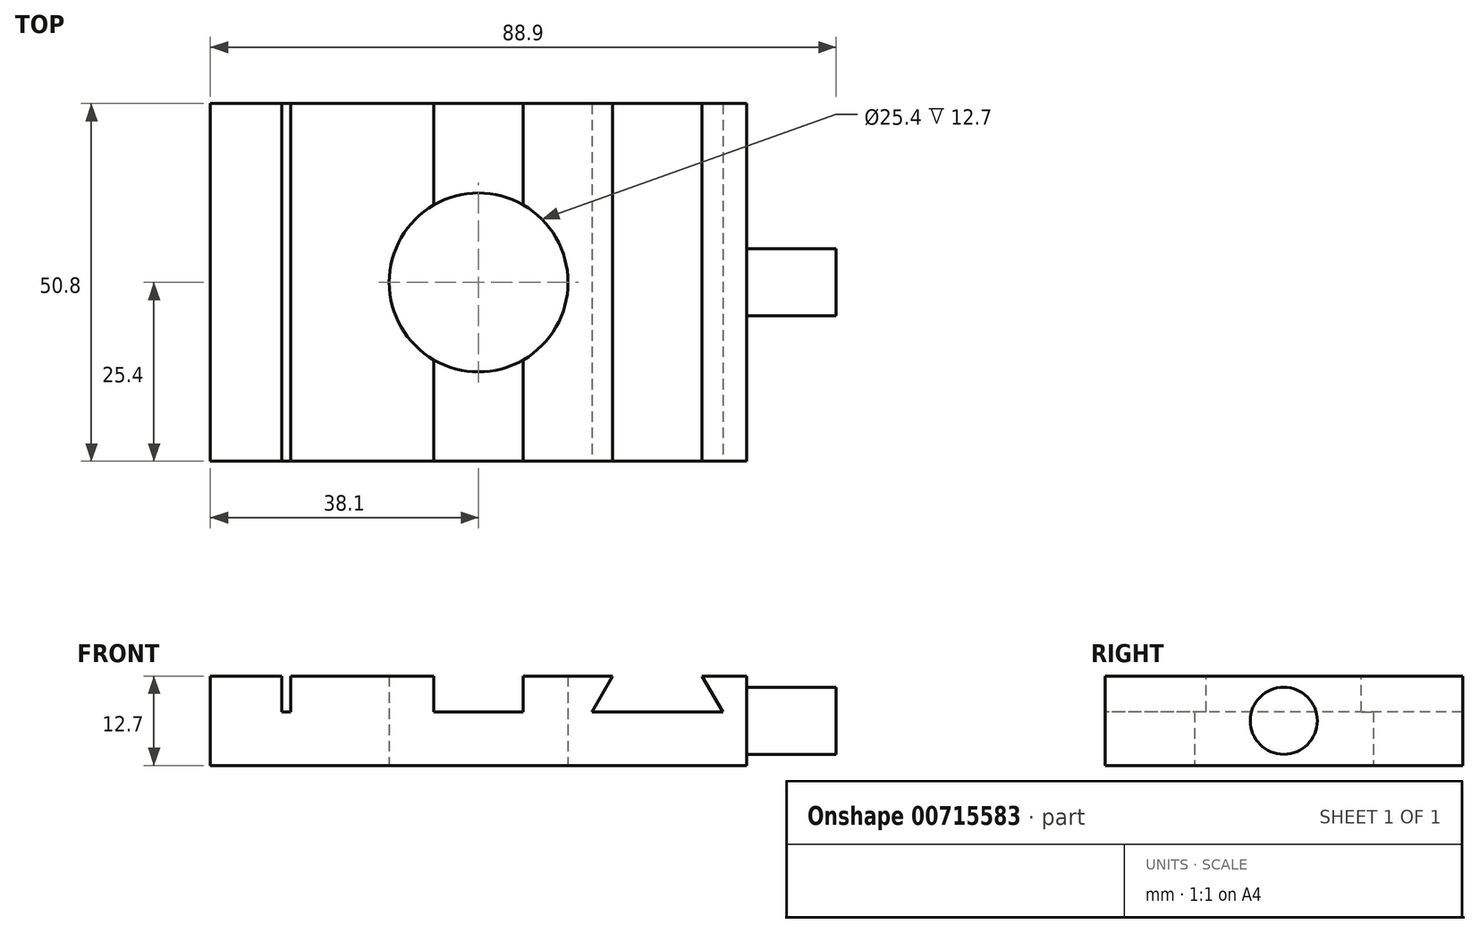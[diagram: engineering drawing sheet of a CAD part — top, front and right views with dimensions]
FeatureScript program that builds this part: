
annotation { "Feature Type Name" : "Feature", "Feature Type Description" : "" }
export const myFeature = defineFeature(function(context is Context, id is Id, definition is map)
    precondition{}
    {
        {
            var Q0;
            Q0=qCreatedBy(makeId("Top.planeOp"),FACE);
            var sketch = newSketch(context, id + "F0", { "sketchPlane" : qUnion([Q0])});
            skLineSegment(sketch, "E0.bottom", {"start": v(-38.1, 25.4) * mm, "end": v(38.1, 25.4) * mm});
            skLineSegment(sketch, "E0.top", {"start": v(-38.1, -25.4) * mm, "end": v(38.1, -25.4) * mm});
            skLineSegment(sketch, "E0.left", {"start": v(-38.1, 25.4) * mm, "end": v(-38.1, -25.4) * mm});
            skLineSegment(sketch, "E0.right", {"start": v(38.1, 25.4) * mm, "end": v(38.1, -25.4) * mm});
            skPoint(sketch, "E0.middle", {"position": v(0, 0) * mm});
            skCircle(sketch, "E1", {"center": v(0, 0) * mm, "radius": 12.7 * mm});
            skSolve(sketch);
        }
        {
            var Q0;
            Q0=makeQuery(id+"F0.imprint","IMPRINT",FACE,{"disambiguationData":[TD([[makeQuery(id+"F0.imprint","IMPRINT",EDGE,{"derivedFrom":sQuery(id+"F0.wireOp",EDGE,"E0.bottom")}),-1.0]])]});
            extrude(context, id + "F1", {"entities" : qUnion([Q0]), "depth" : 12.7 * mm, "offsetDistance" : 25.4 * mm});
        }
        {
            var Q0;
            Q0=makeQuery(id+"F1.opExtrude","CAP_FACE",FACE,{"disambiguationData":[OSD([sQuery(id+"F0.wireOp",EDGE,"E0.bottom"),sQuery(id+"F0.wireOp",EDGE,"E0.top"),sQuery(id+"F0.wireOp",EDGE,"E0.left"),sQuery(id+"F0.wireOp",EDGE,"E0.right"),sQuery(id+"F0.wireOp",EDGE,"E1")])],"isStart":false});
            var sketch = newSketch(context, id + "F2", { "sketchPlane" : qUnion([Q0])});
            skLineSegment(sketch, "E2.bottom", {"start": v(-27.94, 25.4) * mm, "end": v(-26.67, 25.4) * mm});
            skLineSegment(sketch, "E2.top", {"start": v(-27.94, -25.4) * mm, "end": v(-26.67, -25.4) * mm});
            skLineSegment(sketch, "E2.left", {"start": v(-27.94, 25.4) * mm, "end": v(-27.94, -25.4) * mm});
            skLineSegment(sketch, "E2.right", {"start": v(-26.67, 25.4) * mm, "end": v(-26.67, -25.4) * mm});
            skLineSegment(sketch, "E3", {"start": v(-6.35, 25.4) * mm, "end": v(-6.35, -25.4) * mm});
            skLineSegment(sketch, "E4", {"start": v(-6.35, -25.4) * mm, "end": v(6.35, -25.4) * mm});
            skLineSegment(sketch, "E5", {"start": v(6.35, -25.4) * mm, "end": v(6.35, 25.4) * mm});
            skLineSegment(sketch, "E6", {"start": v(6.35, 25.4) * mm, "end": v(-6.35, 25.4) * mm});
            skPoint(sketch, "E7", {"position": v(0, 0) * mm});
            skLineSegment(sketch, "E8", {"start": v(0, 25.4) * mm, "end": v(0, -25.4) * mm, "construction": true});
            skSolve(sketch);
        }
        {
            var Q0;
            Q0=makeQuery(id+"F2.imprint","IMPRINT",FACE,{"disambiguationData":[TD([[makeQuery(id+"F2.imprint","IMPRINT",EDGE,{"derivedFrom":sQuery(id+"F2.wireOp",EDGE,"E2.bottom")}),-1.0]])]});
            var Q1;
            {var subQ0=sQuery(id+"F2.wireOp",EDGE,"E4");Q1=makeQuery(id+"F2.imprint","IMPRINT",FACE,{"disambiguationData":[TD([[makeQuery(id+"F2.imprint","IMPRINT",EDGE,{"derivedFrom":subQ0}),1.0]])]});}
            var Q2;
            {var subQ0=sQuery(id+"F2.wireOp",EDGE,"E6");Q2=makeQuery(id+"F2.imprint","IMPRINT",FACE,{"disambiguationData":[TD([[makeQuery(id+"F2.imprint","IMPRINT",EDGE,{"derivedFrom":subQ0}),-1.0]])]});}
            extrude(context, id + "F3", {"entities" : qUnion([Q0, Q1, Q2]), "operationType" : NewBodyOperationType.REMOVE, "oppositeDirection" : true, "depth" : 5.08 * mm, "offsetDistance" : 25.4 * mm});
        }
        {
            var Q0;
            Q0=makeQuery(id+"F1.opExtrude","SWEPT_FACE",FACE,{"disambiguationData":[OSD([sQuery(id+"F0.wireOp",EDGE,"E0.top")])]});
            var sketch = newSketch(context, id + "F4", { "sketchPlane" : qUnion([Q0])});
            skLineSegment(sketch, "E9", {"start": v(19.05, 12.7) * mm, "end": v(16.12, 7.62) * mm});
            skLineSegment(sketch, "E10", {"start": v(16.12, 7.62) * mm, "end": v(34.68, 7.62) * mm});
            skLineSegment(sketch, "E11", {"start": v(34.68, 7.62) * mm, "end": v(31.75, 12.7) * mm});
            skLineSegment(sketch, "E12", {"start": v(31.75, 12.7) * mm, "end": v(19.05, 12.7) * mm});
            skLineSegment(sketch, "E13", {"start": v(25.4, 7.62) * mm, "end": v(25.4, 12.7) * mm, "construction": true});
            skSolve(sketch);
        }
        {
            var Q0;
            Q0=makeQuery(id+"F4.imprint","IMPRINT",FACE,{"disambiguationData":[TD([[makeQuery(id+"F4.imprint","IMPRINT",EDGE,{"derivedFrom":sQuery(id+"F4.wireOp",EDGE,"E9")}),1.0]])]});
            extrude(context, id + "F5", {"entities" : qUnion([Q0]), "operationType" : NewBodyOperationType.REMOVE, "endBound" : BoundingType.THROUGH_ALL, "oppositeDirection" : true, "depth" : 25.4 * mm, "offsetDistance" : 25.4 * mm});
        }
        {
            var Q0;
            Q0=makeQuery(id+"F1.opExtrude","SWEPT_FACE",FACE,{"disambiguationData":[OSD([sQuery(id+"F0.wireOp",EDGE,"E0.right")])]});
            var sketch = newSketch(context, id + "F6", { "sketchPlane" : qUnion([Q0])});
            skCircle(sketch, "E14", {"center": v(0, 6.35) * mm, "radius": 4.76 * mm});
            skPoint(sketch, "E14.centerSnap0", {"position": v(0, 12.7) * mm});
            skPoint(sketch, "E14.centerSnap1", {"position": v(-25.4, 6.35) * mm});
            skSolve(sketch);
        }
        {
            var Q0;
            Q0=makeQuery(id+"F6.imprint","IMPRINT",FACE,{"disambiguationData":[TD([[makeQuery(id+"F6.imprint","IMPRINT",EDGE,{"derivedFrom":sQuery(id+"F6.wireOp",EDGE,"E14")}),1.0]])]});
            extrude(context, id + "F7", {"entities" : qUnion([Q0]), "operationType" : NewBodyOperationType.ADD, "depth" : 12.7 * mm, "offsetDistance" : 25.4 * mm});
        }
    });
